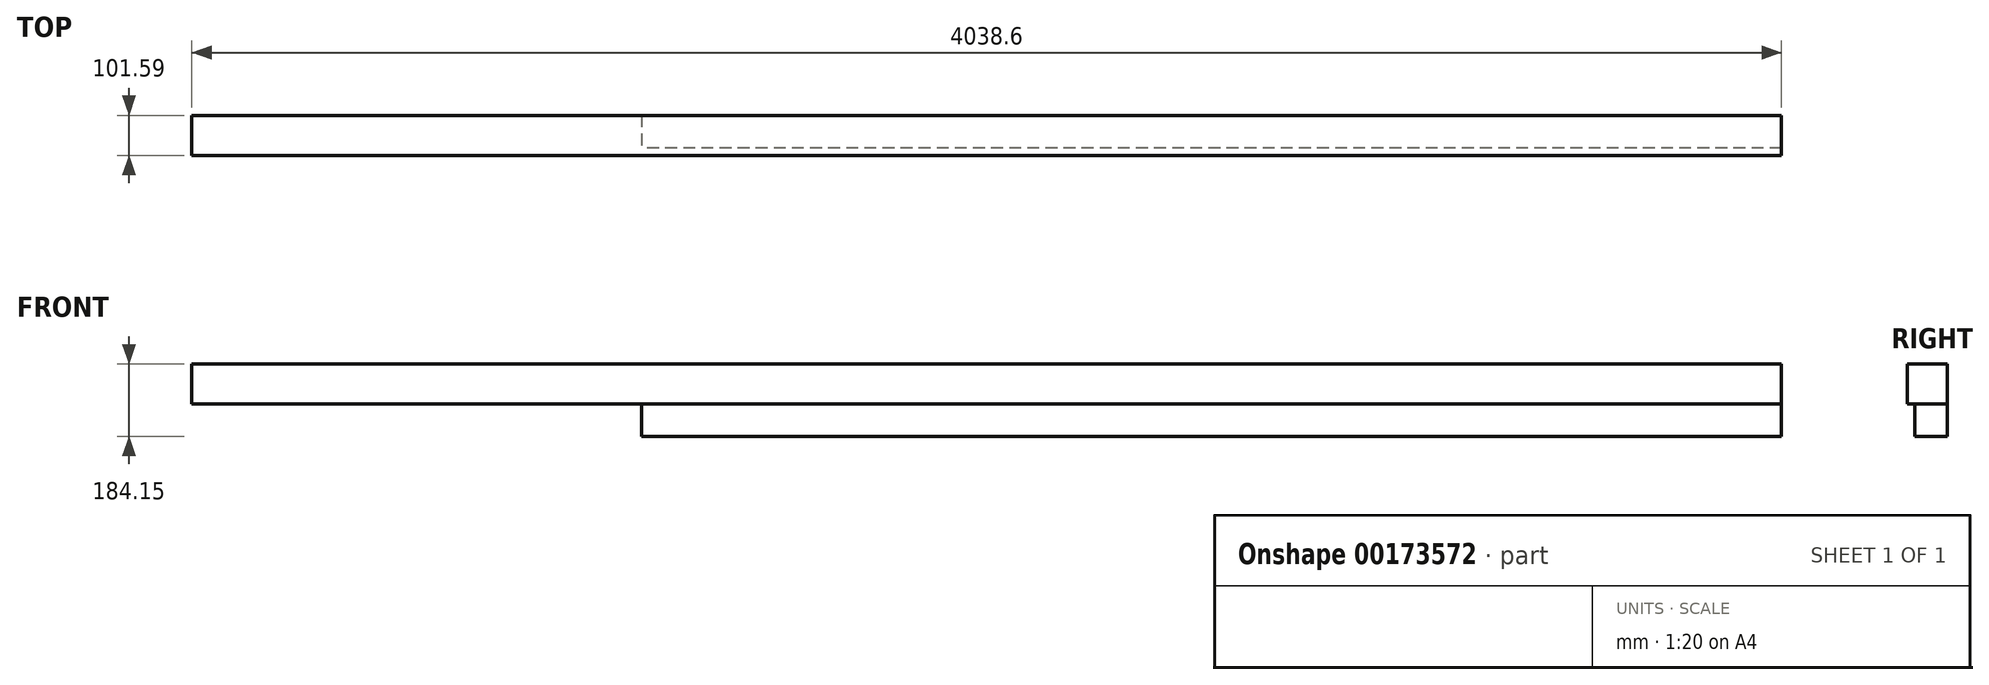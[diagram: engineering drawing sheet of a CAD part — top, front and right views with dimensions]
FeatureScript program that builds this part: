
annotation { "Feature Type Name" : "Feature", "Feature Type Description" : "" }
export const myFeature = defineFeature(function(context is Context, id is Id, definition is map)
    precondition{}
    {
        {
            var Q0;
            Q0=qCreatedBy(makeId("Right.planeOp"),FACE);
            var sketch = newSketch(context, id + "F0", { "sketchPlane" : qUnion([Q0])});
            skLineSegment(sketch, "E0.bottom", {"start": v(41.28, 41.28) * mm, "end": v(-41.28, 41.28) * mm});
            skLineSegment(sketch, "E0.top", {"start": v(41.28, -41.28) * mm, "end": v(-41.28, -41.28) * mm});
            skLineSegment(sketch, "E0.left", {"start": v(41.28, 41.28) * mm, "end": v(41.28, -41.28) * mm});
            skLineSegment(sketch, "E0.right", {"start": v(-41.28, 41.28) * mm, "end": v(-41.28, -41.28) * mm});
            skPoint(sketch, "E0.middle", {"position": v(0, 0) * mm});
            skLineSegment(sketch, "E1.bottom", {"start": v(41.28, 41.28) * mm, "end": v(-60.32, 41.28) * mm});
            skLineSegment(sketch, "E1.top", {"start": v(41.28, 142.88) * mm, "end": v(-60.33, 142.88) * mm});
            skLineSegment(sketch, "E1.left", {"start": v(41.28, 41.28) * mm, "end": v(41.28, 142.88) * mm});
            skLineSegment(sketch, "E1.right", {"start": v(-60.32, 41.28) * mm, "end": v(-60.33, 142.88) * mm});
            skSolve(sketch);
        }
        {
            var Q0;
            Q0=makeQuery(id+"F0.imprint","IMPRINT",FACE,{"disambiguationData":[TD([[makeQuery(id+"F0.imprint","IMPRINT",EDGE,{"derivedFrom":sQuery(id+"F0.wireOp",EDGE,"E0.top")}),-1.0]])]});
            extrude(context, id + "F1", {"entities" : qUnion([Q0]), "depth" : 2895.6 * mm});
        }
        {
            var Q0;
            Q0=makeQuery(id+"F0.imprint","IMPRINT",FACE,{"disambiguationData":[TD([[makeQuery(id+"F0.imprint","IMPRINT",EDGE,{"derivedFrom":sQuery(id+"F0.wireOp",EDGE,"E1.top")}),1.0]])]});
            var Q1;
            Q1=makeQuery(id+"F1.opExtrude","CAP_FACE",FACE,{"disambiguationData":[OSD([sQuery(id+"F0.wireOp",EDGE,"E0.top"),sQuery(id+"F0.wireOp",EDGE,"E0.left"),sQuery(id+"F0.wireOp",EDGE,"E0.right"),sQuery(id+"F0.wireOp",EDGE,"CAPq7vC2-claq-VLv2-iKXr-gytnsDIgcFwj.bottom")])],"isStart":false});
            var Q2;
            Q2=makeQuery(id+"F1.opExtrude","CAP_FACE",FACE,{"disambiguationData":[OSD([sQuery(id+"F0.wireOp",EDGE,"E0.top"),sQuery(id+"F0.wireOp",EDGE,"E0.left"),sQuery(id+"F0.wireOp",EDGE,"E0.right"),sQuery(id+"F0.wireOp",EDGE,"E1.bottom")])],"isStart":false});
            extrude(context, id + "F2", {"entities" : qUnion([Q0]), "oppositeDirection" : true, "endBoundEntityFace" : qUnion([Q1]), "depth" : 1143 * mm, "hasSecondDirection" : true, "secondDirectionBound" : SecondDirectionBoundingType.UP_TO_SURFACE, "secondDirectionOppositeDirection" : false, "secondDirectionBoundEntityFace" : qUnion([Q2]), "secondDirectionDepth" : 1828.8 * mm});
        }
    });
